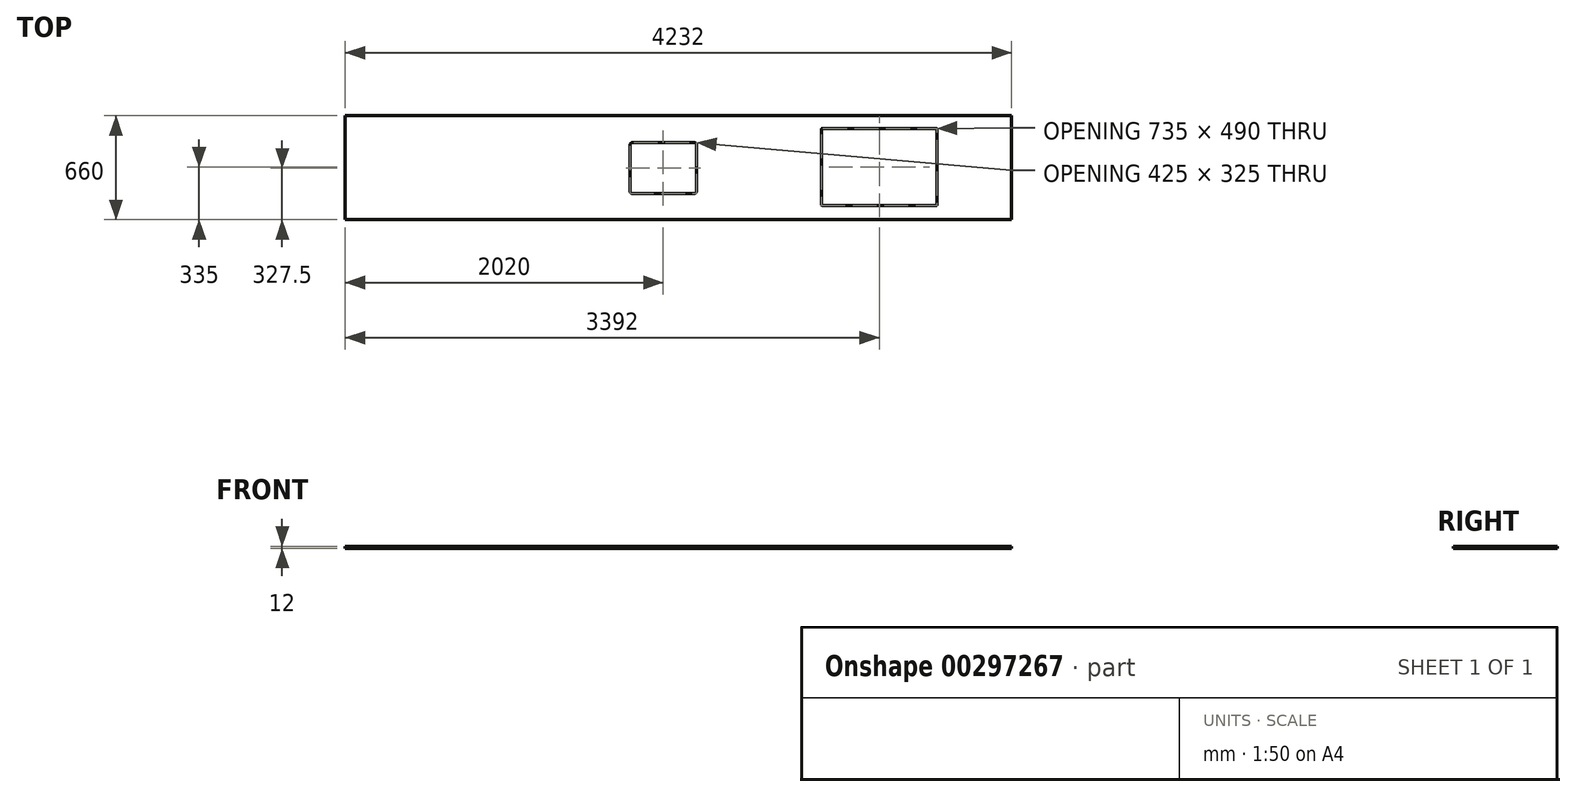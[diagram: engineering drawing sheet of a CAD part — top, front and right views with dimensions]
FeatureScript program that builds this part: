
annotation { "Feature Type Name" : "Feature", "Feature Type Description" : "" }
export const myFeature = defineFeature(function(context is Context, id is Id, definition is map)
    precondition{}
    {
        {
            var Q0;
            Q0=qCreatedBy(makeId("Top.planeOp"),FACE);
            var sketch = newSketch(context, id + "F0", { "sketchPlane" : qUnion([Q0])});
            skLineSegment(sketch, "E0.bottom", {"start": v(-2116, 330) * mm, "end": v(2116, 330) * mm});
            skLineSegment(sketch, "E0.top", {"start": v(-2116, -330) * mm, "end": v(2116, -330) * mm});
            skLineSegment(sketch, "E0.left", {"start": v(-2116, 330) * mm, "end": v(-2116, -330) * mm});
            skLineSegment(sketch, "E0.right", {"start": v(2116, 330) * mm, "end": v(2116, -330) * mm});
            skPoint(sketch, "E0.middle", {"position": v(0, 0) * mm});
            skSolve(sketch);
        }
        {
            var Q0;
            Q0 = qSketchRegion(id + "F0", true);
            extrude(context, id + "F1", {"entities" : qUnion([Q0]), "depth" : 12 * mm, "offsetDistance" : 25 * mm});
        }
        {
            var Q0;
            Q0=makeQuery(id+"F1.opExtrude","CAP_FACE",FACE,{"disambiguationData":[OSD([sQuery(id+"F0.wireOp",EDGE,"E0.bottom"),sQuery(id+"F0.wireOp",EDGE,"E0.top"),sQuery(id+"F0.wireOp",EDGE,"E0.left"),sQuery(id+"F0.wireOp",EDGE,"E0.right")])],"isStart":false});
            var sketch = newSketch(context, id + "F2", { "sketchPlane" : qUnion([Q0])});
            skLineSegment(sketch, "E1.bottom", {"start": v(-290.5, 160) * mm, "end": v(98.5, 160) * mm});
            skLineSegment(sketch, "E1.top", {"start": v(-290.5, -165) * mm, "end": v(98.5, -165) * mm});
            skLineSegment(sketch, "E1.left", {"start": v(-308.5, 142) * mm, "end": v(-308.5, -147) * mm});
            skLineSegment(sketch, "E1.right", {"start": v(116.5, 142) * mm, "end": v(116.5, -147) * mm});
            skLineSegment(sketch, "E2.bottom", {"start": v(913.5, 250) * mm, "end": v(1638.5, 250) * mm});
            skLineSegment(sketch, "E2.top", {"start": v(913.5, -240) * mm, "end": v(1638.5, -240) * mm});
            skLineSegment(sketch, "E2.left", {"start": v(908.5, 245) * mm, "end": v(908.5, -235) * mm});
            skLineSegment(sketch, "E2.right", {"start": v(1643.5, 245) * mm, "end": v(1643.5, -235) * mm});
            skPoint(sketch, "E3.visualSharp", {"position": v(908.5, 250) * mm});
            skArc(sketch, "E3.filletArc", {"start": v(913.5, 250) * mm, "mid": v(909.96, 248.54) * mm, "end": v(908.5, 245) * mm});
            skPoint(sketch, "E4.visualSharp", {"position": v(1643.5, 250) * mm});
            skArc(sketch, "E4.filletArc", {"start": v(1643.5, 245) * mm, "mid": v(1642.04, 248.54) * mm, "end": v(1638.5, 250) * mm});
            skPoint(sketch, "E5.visualSharp", {"position": v(1643.5, -240) * mm});
            skArc(sketch, "E5.filletArc", {"start": v(1638.5, -240) * mm, "mid": v(1642.04, -238.54) * mm, "end": v(1643.5, -235) * mm});
            skPoint(sketch, "E6.visualSharp", {"position": v(908.5, -240) * mm});
            skArc(sketch, "E6.filletArc", {"start": v(908.5, -235) * mm, "mid": v(909.96, -238.54) * mm, "end": v(913.5, -240) * mm});
            skLineSegment(sketch, "E7", {"start": v(-96, 160) * mm, "end": v(-96, -165) * mm, "construction": true});
            skLineSegment(sketch, "E8", {"start": v(-96, -165) * mm, "end": v(-96, -115.42) * mm, "construction": true});
            skPoint(sketch, "E9.visualSharp", {"position": v(-308.5, 160) * mm});
            skArc(sketch, "E9.filletArc", {"start": v(-290.5, 160) * mm, "mid": v(-303.23, 154.73) * mm, "end": v(-308.5, 142) * mm});
            skPoint(sketch, "E10.visualSharp", {"position": v(116.5, 160) * mm});
            skArc(sketch, "E10.filletArc", {"start": v(116.5, 142) * mm, "mid": v(111.23, 154.73) * mm, "end": v(98.5, 160) * mm});
            skPoint(sketch, "E11.visualSharp", {"position": v(116.5, -165) * mm});
            skArc(sketch, "E11.filletArc", {"start": v(98.5, -165) * mm, "mid": v(111.23, -159.73) * mm, "end": v(116.5, -147) * mm});
            skPoint(sketch, "E12.visualSharp", {"position": v(-308.5, -165) * mm});
            skArc(sketch, "E12.filletArc", {"start": v(-308.5, -147) * mm, "mid": v(-303.23, -159.73) * mm, "end": v(-290.5, -165) * mm});
            skSolve(sketch);
        }
        {
            var Q0;
            Q0 = qSketchRegion(id + "F2", true);
            extrude(context, id + "F3", {"entities" : qUnion([Q0]), "operationType" : NewBodyOperationType.REMOVE, "oppositeDirection" : true, "depth" : 30 * mm});
        }
    });
